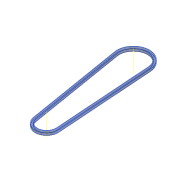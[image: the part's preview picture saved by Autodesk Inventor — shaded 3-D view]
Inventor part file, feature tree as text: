
AUTODESK INVENTOR PART (.ipt)
format: ipt  version: 2013 (Build 170138000, 138)  size: 158,208 bytes
history: native  units: mm
features: other x5, plane x2, pattern_linear x1
ambient origin geometry x8: Origin, YZ Plane, XZ Plane, XY Plane, X Axis, Y Axis, Z Axis, Center Point
bodies: Solid1 (feature_tree), Solid (feature_tree)
feature tree (8):
  other  "Work Axis1"
  other  "Work Axis2"
  plane  "Work Plane2"
  plane  "Work Plane3"
  other  "Path"
  other  "Section Plane"
  pattern_linear  "Strand Pattern"  Spacing1=0.0mm  [1 undecoded]
  other  "Section Sketch"
note: 1 required parameter value undecoded (feature->parameter linkage not recoverable at this tier; creation-order binding heuristic only, values carry confidence <= 0.55)
